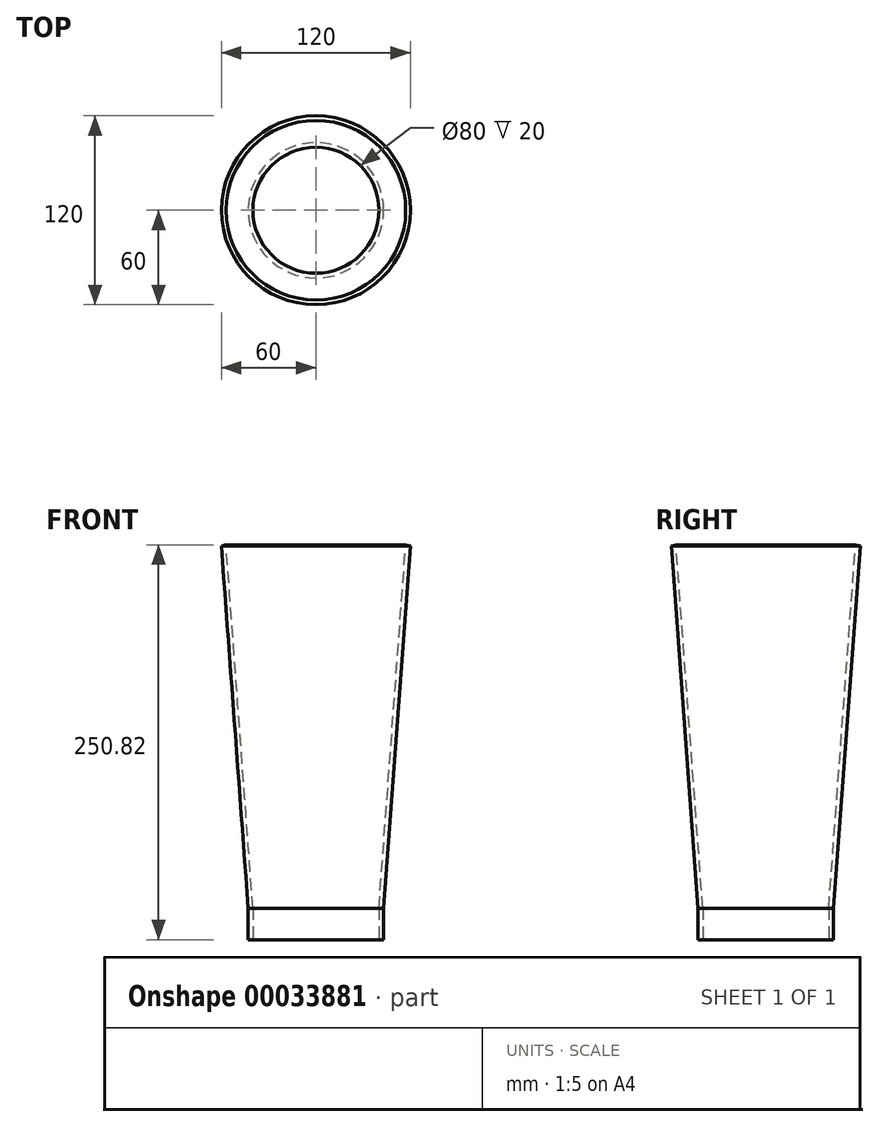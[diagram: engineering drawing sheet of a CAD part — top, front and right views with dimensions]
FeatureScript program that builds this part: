
annotation { "Feature Type Name" : "Feature", "Feature Type Description" : "" }
export const myFeature = defineFeature(function(context is Context, id is Id, definition is map)
    precondition{}
    {
        {
            var Q0;
            Q0=qCreatedBy(makeId("Front.planeOp"),FACE);
            var sketch = newSketch(context, id + "F0", { "sketchPlane" : qUnion([Q0])});
            skLineSegment(sketch, "E0", {"start": v(40, 0) * mm, "end": v(40, 20) * mm});
            skLineSegment(sketch, "E1", {"start": v(40, 20) * mm, "end": v(57.05, 250.82) * mm});
            skLineSegment(sketch, "E2.0", {"start": v(43, 19.89) * mm, "end": v(60, 250) * mm});
            skLineSegment(sketch, "E2.1", {"start": v(43, 0) * mm, "end": v(43, 19.89) * mm});
            skLineSegment(sketch, "E3", {"start": v(40, 0) * mm, "end": v(40, 0) * mm});
            skLineSegment(sketch, "E4", {"start": v(44.43, -0.57) * mm, "end": v(44.43, -0.57) * mm});
            skLineSegment(sketch, "E5", {"start": v(43, 0) * mm, "end": v(40, 0) * mm});
            skLineSegment(sketch, "E6", {"start": v(57.05, 250.82) * mm, "end": v(60, 250) * mm});
            skLineSegment(sketch, "E7", {"start": v(0, 0) * mm, "end": v(0, 120.74) * mm, "construction": true});
            skSolve(sketch);
        }
        {
            var Q0;
            Q0 = qSketchRegion(id + "F0", true);
            var Q1;
            Q1=sQuery(id+"F0.wireOp",EDGE,"E7");
            revolve(context, id + "F1", {"entities" : qUnion([Q0]), "axis" : qUnion([Q1]), "revolveType" : RevolveType.FULL});
        }
    });
